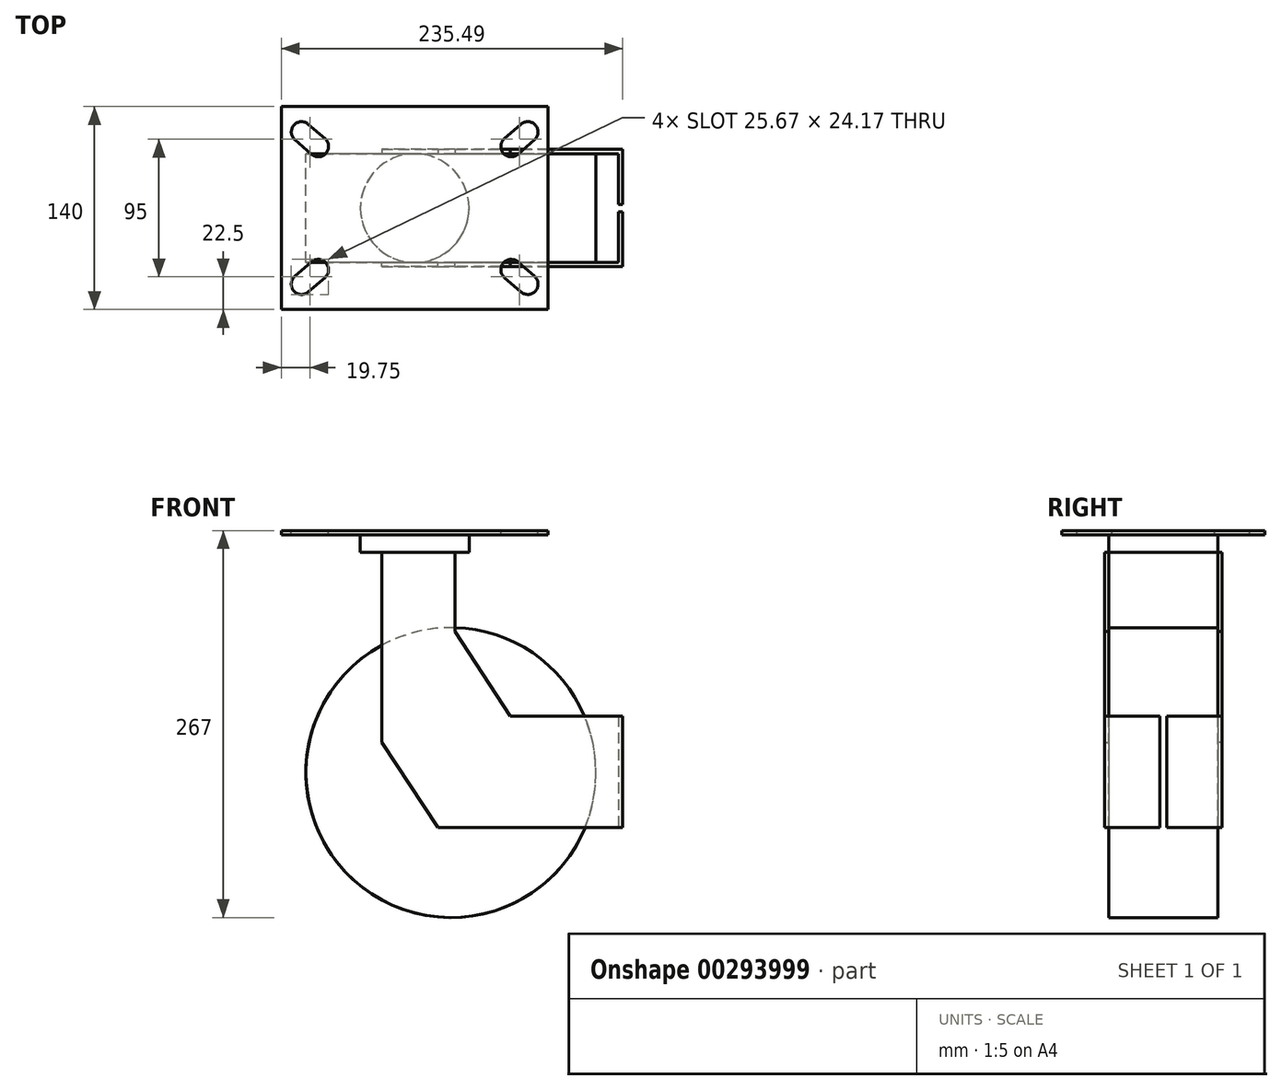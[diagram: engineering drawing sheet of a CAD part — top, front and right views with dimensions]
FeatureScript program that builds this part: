
annotation { "Feature Type Name" : "Feature", "Feature Type Description" : "" }
export const myFeature = defineFeature(function(context is Context, id is Id, definition is map)
    precondition{}
    {
        {
            var Q0;
            Q0=qCreatedBy(makeId("Top.planeOp"),FACE);
            var sketch = newSketch(context, id + "F0", { "sketchPlane" : qUnion([Q0])});
            skLineSegment(sketch, "E0.bottom", {"start": v(-92, 70) * mm, "end": v(92, 70) * mm});
            skLineSegment(sketch, "E0.top", {"start": v(-92, -70) * mm, "end": v(92, -70) * mm});
            skLineSegment(sketch, "E0.left", {"start": v(-92, 70) * mm, "end": v(-92, -70) * mm});
            skLineSegment(sketch, "E0.right", {"start": v(92, 70) * mm, "end": v(92, -70) * mm});
            skPoint(sketch, "E0.middle", {"position": v(0, 0) * mm});
            skPoint(sketch, "E1", {"position": v(-92, 0) * mm});
            skPoint(sketch, "E2", {"position": v(0, 70) * mm});
            skLineSegment(sketch, "E3.bottom", {"start": v(-66.5, 42.5) * mm, "end": v(66.5, 42.5) * mm, "construction": true});
            skLineSegment(sketch, "E3.top", {"start": v(-66.5, -42.5) * mm, "end": v(66.5, -42.5) * mm, "construction": true});
            skLineSegment(sketch, "E3.left", {"start": v(-66.5, 42.5) * mm, "end": v(-66.5, -42.5) * mm, "construction": true});
            skLineSegment(sketch, "E3.right", {"start": v(66.5, 42.5) * mm, "end": v(66.5, -42.5) * mm, "construction": true});
            skLineSegment(sketch, "E4.bottom", {"start": v(-78, 52.5) * mm, "end": v(78, 52.5) * mm, "construction": true});
            skLineSegment(sketch, "E4.top", {"start": v(-78, -52.5) * mm, "end": v(78, -52.5) * mm, "construction": true});
            skLineSegment(sketch, "E4.left", {"start": v(-78, 52.5) * mm, "end": v(-78, -52.5) * mm, "construction": true});
            skLineSegment(sketch, "E4.right", {"start": v(78, 52.5) * mm, "end": v(78, -52.5) * mm, "construction": true});
            skArc(sketch, "E5", {"start": v(-73.34, 57.86) * mm, "mid": v(-83.36, 57.16) * mm, "end": v(-82.66, 47.14) * mm});
            skArc(sketch, "E6", {"start": v(-71.16, 37.14) * mm, "mid": v(-61.14, 37.84) * mm, "end": v(-61.84, 47.86) * mm});
            skArc(sketch, "E7", {"start": v(82.66, 47.14) * mm, "mid": v(83.36, 57.16) * mm, "end": v(73.34, 57.86) * mm});
            skArc(sketch, "E8", {"start": v(61.84, 47.86) * mm, "mid": v(61.14, 37.84) * mm, "end": v(71.16, 37.14) * mm});
            skArc(sketch, "E9", {"start": v(71.16, -37.14) * mm, "mid": v(61.14, -37.84) * mm, "end": v(61.84, -47.86) * mm});
            skArc(sketch, "E10", {"start": v(73.34, -57.86) * mm, "mid": v(83.36, -57.16) * mm, "end": v(82.66, -47.14) * mm});
            skArc(sketch, "E11", {"start": v(-61.84, -47.86) * mm, "mid": v(-61.14, -37.84) * mm, "end": v(-71.16, -37.14) * mm});
            skArc(sketch, "E12", {"start": v(-82.66, -47.14) * mm, "mid": v(-83.36, -57.16) * mm, "end": v(-73.34, -57.86) * mm});
            skLineSegment(sketch, "E13", {"start": v(-73.34, 57.86) * mm, "end": v(-61.84, 47.86) * mm});
            skLineSegment(sketch, "E14", {"start": v(-82.66, 47.14) * mm, "end": v(-71.16, 37.14) * mm});
            skLineSegment(sketch, "E15", {"start": v(73.34, 57.86) * mm, "end": v(61.84, 47.86) * mm});
            skLineSegment(sketch, "E16", {"start": v(82.66, 47.14) * mm, "end": v(71.16, 37.14) * mm});
            skLineSegment(sketch, "E17", {"start": v(61.84, -47.86) * mm, "end": v(73.34, -57.86) * mm});
            skLineSegment(sketch, "E18", {"start": v(71.16, -37.14) * mm, "end": v(82.66, -47.14) * mm});
            skLineSegment(sketch, "E19", {"start": v(-61.84, -47.86) * mm, "end": v(-73.34, -57.86) * mm});
            skLineSegment(sketch, "E20", {"start": v(-71.16, -37.14) * mm, "end": v(-82.66, -47.14) * mm});
            skSolve(sketch);
        }
        {
            var Q0;
            Q0=qSketchRegion(id+"F0",true);
            extrude(context, id + "F1", {"entities" : qUnion([Q0]), "oppositeDirection" : true, "depth" : 3 * mm});
        }
        {
            var Q0;
            Q0=makeQuery(id+"F1.opExtrude","CAP_FACE",FACE,{"disambiguationData":[OSD([sQuery(id+"F0.wireOp",EDGE,"E0.bottom"),sQuery(id+"F0.wireOp",EDGE,"E0.top"),sQuery(id+"F0.wireOp",EDGE,"E0.left"),sQuery(id+"F0.wireOp",EDGE,"E0.right"),sQuery(id+"F0.wireOp",EDGE,"E5"),sQuery(id+"F0.wireOp",EDGE,"E6"),sQuery(id+"F0.wireOp",EDGE,"E7"),sQuery(id+"F0.wireOp",EDGE,"E8"),sQuery(id+"F0.wireOp",EDGE,"E9"),sQuery(id+"F0.wireOp",EDGE,"E10"),sQuery(id+"F0.wireOp",EDGE,"E11"),sQuery(id+"F0.wireOp",EDGE,"E12"),sQuery(id+"F0.wireOp",EDGE,"E13"),sQuery(id+"F0.wireOp",EDGE,"E14"),sQuery(id+"F0.wireOp",EDGE,"E15"),sQuery(id+"F0.wireOp",EDGE,"E16"),sQuery(id+"F0.wireOp",EDGE,"E17"),sQuery(id+"F0.wireOp",EDGE,"E18"),sQuery(id+"F0.wireOp",EDGE,"E19"),sQuery(id+"F0.wireOp",EDGE,"E20")])],"isStart":false});
            var sketch = newSketch(context, id + "F2", { "sketchPlane" : qUnion([Q0])});
            skCircle(sketch, "E21", {"center": v(0, 0) * mm, "radius": 37.5 * mm});
            skSolve(sketch);
        }
        {
            var Q0;
            Q0=qSketchRegion(id+"F2",true);
            extrude(context, id + "F3", {"entities" : qUnion([Q0]), "operationType" : NewBodyOperationType.ADD, "depth" : 12 * mm});
        }
        {
            var Q0;
            Q0=qCreatedBy(makeId("Top.planeOp"),FACE);
            cPlane(context, id + "F4", {"entities" : qUnion([Q0]), "cplaneType" : CPlaneType.OFFSET, "offset" : 167 * mm, "oppositeDirection" : true, "width" : 150 * mm, "height" : 150 * mm});
        }
        {
            var Q0;
            Q0=qCreatedBy(makeId("Right.planeOp"),FACE);
            cPlane(context, id + "F5", {"entities" : qUnion([Q0]), "cplaneType" : CPlaneType.OFFSET, "offset" : 25 * mm, "width" : 150 * mm, "height" : 150 * mm});
        }
        {
            var Q0;
            Q0=qCreatedBy(makeId("Front.planeOp"),FACE);
            var sketch = newSketch(context, id + "F6", { "sketchPlane" : qUnion([Q0])});
            skCircle(sketch, "E22", {"center": v(25, -167) * mm, "radius": 100 * mm});
            skSolve(sketch);
        }
        {
            var Q0;
            Q0=qSketchRegion(id+"F6",true);
            extrude(context, id + "F7", {"entities" : qUnion([Q0]), "endBound" : BoundingType.SYMMETRIC, "depth" : 75 * mm});
        }
        {
            var Q0;
            Q0=makeQuery(id+"F7.opExtrude","CAP_FACE",FACE,{"disambiguationData":[OSD([sQuery(id+"F6.wireOp",EDGE,"E22")])],"isStart":false});
            var sketch = newSketch(context, id + "F8", { "sketchPlane" : qUnion([Q0])});
            skLineSegment(sketch, "E23.0", {"start": v(37.5, -15) * mm, "end": v(-37.5, -15) * mm, "construction": true});
            skCircle(sketch, "E24.0", {"center": v(25, -167) * mm, "radius": 100 * mm, "construction": true});
            skLineSegment(sketch, "E25", {"start": v(-22.7, -15) * mm, "end": v(-22.7, -146.05) * mm});
            skLineSegment(sketch, "E26", {"start": v(-22.7, -146.05) * mm, "end": v(16.03, -204.78) * mm});
            skLineSegment(sketch, "E27", {"start": v(16.03, -204.78) * mm, "end": v(143.5, -204.78) * mm});
            skLineSegment(sketch, "E28", {"start": v(143.5, -204.78) * mm, "end": v(143.5, -127.93) * mm});
            skLineSegment(sketch, "E29", {"start": v(143.5, -127.93) * mm, "end": v(66.02, -127.93) * mm});
            skLineSegment(sketch, "E30", {"start": v(66.02, -127.93) * mm, "end": v(27.67, -69.79) * mm});
            skLineSegment(sketch, "E31", {"start": v(27.67, -69.79) * mm, "end": v(27.67, -15) * mm});
            skLineSegment(sketch, "E32", {"start": v(27.67, -15) * mm, "end": v(-22.7, -15) * mm});
            skSolve(sketch);
        }
        {
            var Q0;
            Q0=qSketchRegion(id+"F8",true);
            extrude(context, id + "F9", {"entities" : qUnion([Q0]), "operationType" : NewBodyOperationType.ADD, "depth" : 3 * mm});
        }
        {
            var Q0;
            {var subQ0=sQuery(id+"F8.wireOp",EDGE,"E28");var subQ1=sQuery(id+"F8.wireOp",EDGE,"E27");var subQ3=sQuery(id+"F8.wireOp",EDGE,"E29");Q0=makeQuery(id+"F9.boolean.opBoolean","SPLIT",FACE,{"disambiguationData":[TD([makeQuery(id+"F9.opExtrude","SWEPT_FACE",FACE,{"disambiguationData":[OSD([subQ1])]})])],"derivedFrom":makeQuery(id+"F9.opExtrude","CAP_FACE",FACE,{"disambiguationData":[OSD([sQuery(id+"F8.wireOp",EDGE,"E25"),sQuery(id+"F8.wireOp",EDGE,"E26"),subQ1,subQ0,subQ3,sQuery(id+"F8.wireOp",EDGE,"E30"),sQuery(id+"F8.wireOp",EDGE,"E31"),sQuery(id+"F8.wireOp",EDGE,"E32")])],"isStart":true})});}
            var sketch = newSketch(context, id + "F10", { "sketchPlane" : qUnion([Q0])});
            skLineSegment(sketch, "E33.0", {"start": v(-143.5, -204.78) * mm, "end": v(-143.5, -127.93) * mm});
            skLineSegment(sketch, "E34", {"start": v(-143.5, -127.93) * mm, "end": v(-140.5, -127.93) * mm});
            skLineSegment(sketch, "E35", {"start": v(-140.5, -127.93) * mm, "end": v(-140.5, -204.78) * mm});
            skLineSegment(sketch, "E36", {"start": v(-140.5, -204.78) * mm, "end": v(-143.5, -204.78) * mm});
            skSolve(sketch);
        }
        {
            var Q0;
            Q0=qSketchRegion(id+"F10",true);
            extrude(context, id + "F11", {"entities" : qUnion([Q0]), "operationType" : NewBodyOperationType.ADD, "depth" : 35 * mm});
        }
        {
            var Q0;
            Q0=makeQuery(id+"F7.opExtrude","SWEPT_BODY",BODY,{"disambiguationData":[OSD([sQuery(id+"F6.wireOp",EDGE,"E22")])]});
            var Q1;
            Q1=qCreatedBy(makeId("Front.planeOp"),FACE);
            mirror(context, id + "F12", {"operationType" : NewBodyOperationType.ADD, "entities" : qUnion([Q0]), "mirrorPlane" : qUnion([Q1])});
        }
    });
